# Revit family: 351_51427
name_source: partatom
category: Plumbing Fixtures
units: mm (PartAtom-declared; Revit-internal decimal feet)

## family parameters
Always vertical = Yes
Cut with Voids When Loaded = No
Part Type = Normal
Room Calculation Point = No
Round Connector Dimension = Use Diameter
Shared = No
Work Plane-Based = No

## types (1)
- 5671007 IDO urinal
    CAT0 = Yes
    CLBTZ = 0 mm  [stored 0 ft]
    CL_Location_5000 = 5000 mm  [stored 16.4042 ft]
    D = 50 mm
    Description = URINAL 340x570x340, water connection behind, drain to wall
    H = 570 mm  [stored 1.87008 ft]
    H2 = 155 mm  [stored 0.50853 ft]
    L = 340 mm  [stored 1.11549 ft]
    QmdConnectorList = 601;D
    R1 = 50 mm  [stored 0.164042 ft]
    URL = http://www.ido.fi
    W1 = 100 mm  [stored 0.328084 ft]
    W1__ve = -100 mm  [stored -0.328084 ft]
    XRefLineVPlnId = 7453
    YRefLineVPlnId = 7456
    magiPartTypeId = 351
    magiProductCode = 5671007 IDO urinal
    magiProductFamilyId = 51427
    magiProductId = 51427

note: [stored X ft] marks values corroborated as IEEE doubles in the binary element streams (Revit-internal decimal feet)

## geometry (parser evidence)
native form markers: Sweep x2
no freeform markers — native parametric forms only
